# Revit family: GIRA_212900
name_source: partatom
category: Elektroinstallationen
revit_build: Autodesk Revit 2017 (Build: 20160225_1515(x64)
units: mm (PartAtom-declared; Revit-internal decimal feet)

## family parameters
Basisbauteil = Fläche
Beim Laden mit Abzugskörper schneiden = Nein
Bemaßung runder Anschluss = Durchmesser verwenden
Beschriftungsausrichtung beibehalten = Nein
Gemeinsam genutzt = Nein
Raumberechnungspunkt = Nein
Teiletyp = Normal

## types (1)
- GIRA_212900
    Andere Bussysteme Text = sonstige
    Anzahl der Ausgänge = 2
    Anzahl der Ausgänge Number = 6
    Ausführung Text = Medienkoppler
    Ausgangsleistung [Watt] = [20:500]
    Bemessungsstrom = 16 A
    Beschreibung = KNX Heizungsaktor 6fach mit Regler  REG plus Merkmale: - Heizungsaktor mit integriertem Raumtemperaturregler zum Schalten elektrothermischer Stellantriebe für Heizungen oder Kühldecken. Ventilausgänge: - Schaltbetrieb oder PWM-Betrieb. - Stellantriebe mit Charakteristik stromlos geöffnet" oder "stromlos geschlossen" ansteuerbar. - Stellantriebe mit Nennspannung 24 V oder 230 V ansteuerbar. - Baustellenbetrieb: Ausgänge manuell bedienbar ohne Busspannung nur mit der Betriebsspannung. - Rückmeldung bei Handbetätigung und im Busbetrieb. - Sperren einzelner Ausgänge per Hand oder Bus. - Überlastsicher, kurzschlusssicher, Fehlermeldung mit LED. - Schutz gegen festsitzende Ventile. - Zwangsstellung. - Unterschiedliche Sollwerte für Zwangsstellung oder Notbetrieb bei Busausfall für Sommer und Winter. - Zyklische Überwachung der Eingangssignale parametrierbar. - Rückmeldung über Bus z. B. bei Ausfall der Ventilspannung, Überlast und Kurzschluss. - Schalten der Heizkreispumpe in Abhängigkeit der Ventilzustände. - Sammelrückmeldung der angeschlossenen Stellantriebe. - Energiesparmodus zum Reduzieren des Energieverbrauchs des Heizungsaktors. Anwendung für Zeiträume (z. B. Sommer) wo kein Wärmebedarf zum Heizen besteht. - Aktivierung des Stellantriebs mit "First-Open-Funktion" bei der Erstinbetriebnahme. - Schnelle Inbetriebnahme durch globale Einstellung der Kanäle. - Kaskadierung mehrerer Heizungsaktoren. - Zurücksetzen von Fehlermeldungen über BUS. - Wärmebedarfsteuerung. - Betriebsstundenzähler pro Kanal. Raumtemperaturregler: - 6 unabhängige Regler. - Steuerung über individuelle Kommunikatiosobjekte für Ein- und Ausgänge. - Wahlweise interne Gruppenkommunikation zur individuellen Zuweisung der Reglerausgänge zu den Ausgangskanälen des Aktors. - Betriebsmodi: Komfort, Standby, Nacht und Frost- Hitzeschutz. - Jedem Betriebsmodus können eigene Temperatur-Sollwerte zugeordnet werden. - Konfiguration der Temperatur-Sollwerte wahlweise relativ (Ableitung aus Basis-Sollwert) oder absolut (unabhängige Solltemperaturen für jeden Betriebsmodus). - Komfortverlängerung durch Präsenztaste, Dauer parametrierbar. - Umschaltung der Betriebsmodi durch 1-Byte-Objekte gemäß der KNX Spezifikation oder durch bis zu 4 einzelne 1-Bit-Objekte. - Statusrückmeldungen konfigurierbar. - Frost- Hitzeschutz-Umschaltung durch Fensterstatus oder durch Frostschutz-Automatik. - Betriebsarten "Heizen", "Kühlen", "Heizen und Kühlen" jeweils mit oder ohne Zusatzstufe. Die Temperatur-Sollwerte für die Zusatzstufe leiten sich durch einen parametrierbaren Stufenabstand aus den Werten der Grundstufe ab. - Je Heiz- oder Kühlstufe sind verschiedene Regelungsarten konfigurierbar: PI-Regelung (stetige oder schaltende PWM) oder 2-Punkt-Regelung (schaltend). - Regelparameter für PI-Regler (falls gewünscht: Proportionalbereich, Nachstellzeit) und 2Punkt-Regler (Hysterese) einstellbar. - Automatisches oder objektorientiertes Umschalten zwischen "Heizen" und "Kühlen". - Raumtemperaturmessung über bis zu zwei externe KNX Temperaturfühler. Abgleich der Temperaturwerte möglich und Messwertbildung der externen Fühler parametrierbar. Abfragezeit der extern empfangenen Temperaturwerte einstellbar. - Die Ist- und Soll-Temperaturen können nach einer parametrierbaren Abweichung auf den Bus (auch zyklisch) ausgegeben werden. - Getrennte oder gemeinsame Stellgrößenausgabe im Heiz- und Kühlbetrieb. Dadurch ein oder zwei Stellgrößenobjekte je Stufe. - Normale oder invertierte Stellgrößenausgabe. - Automatisches Senden und Zykluszeit für Stellgrößenausgabe parametrierbar. - Stellgrößenbegrenzung möglich. - Fußbodentemperaturbegrenzung im Heizbetrieb möglich. - Solltemperaturbegrenzung im Kühlbetrieb möglich.  Hinweise : - An allen Ausgängen müssen Ventile mit der gleichen Betriebsspannung angeschlossen werden. - VDE-Zulassung gemäß EN 60669-1, EN 60669-2-1. - Montage auf DIN-Hutschiene."
    Breite in Teilungseinheiten = 4
    Breite in Teilungseinheiten Number = 4
    Busmodul abnehmbar = Nein
    Bussystem Funkbus YesNo = Nein
    Bussystem KNX YesNo = Ja
    Bussystem KNX-Funk YesNo = Nein
    Bussystem LON YesNo = Nein
    Bussystem Powernet YesNo = Nein
    Demontageschutz = Nein
    Frequenz [Hz] = [50:60]
    Funk bidirektional = Nein
    GTIN = 4010337032915
    HAN = 212900
    Handschaltung = Ja
    Hersteller = Gira
    IR-Schnittstelle = Nein
    Lastart = universal
    Leistungszusatz verwendbar = Nein
    Max. Anzahl der Jalousieausgänge = 4
    Max. Anzahl der Schaltausgänge = 8
    Max. Schaltstrom (Ohmsche Last) = 2 A
    Mit Busankopplung YesNo = Nein
    Mit LED-Anzeige = Nein
    Mit LED-Anzeige YesNo = Nein
    Modulare Erweiterungsmöglichkeit = Ja
    Montageart Text = REG
    Nebenstelleneingang = Ja
    Parallel-Betrieb möglich = Nein
    Schaltspannung [Volt] = [110:230]
    Schutzart (IP) Text = IP20
    Spannung [Volt] = [230:230]
    Stellgröße schaltend = Nein
    Stellgröße stetig = Ja
    Typname = Heizungsaktor 6f Regler KNX REG
    URL = https://www.gira.de
    Ventilschutzfunktion = Nein
    Vor Ort-/Handbedienung = Ja
    Vor Ort-/Handbedienung YesNo = Ja
    Vorgabe-Ansicht = 1219 mm

## geometry (parser evidence)
native form markers: Sweep x3
no freeform markers — native parametric forms only
